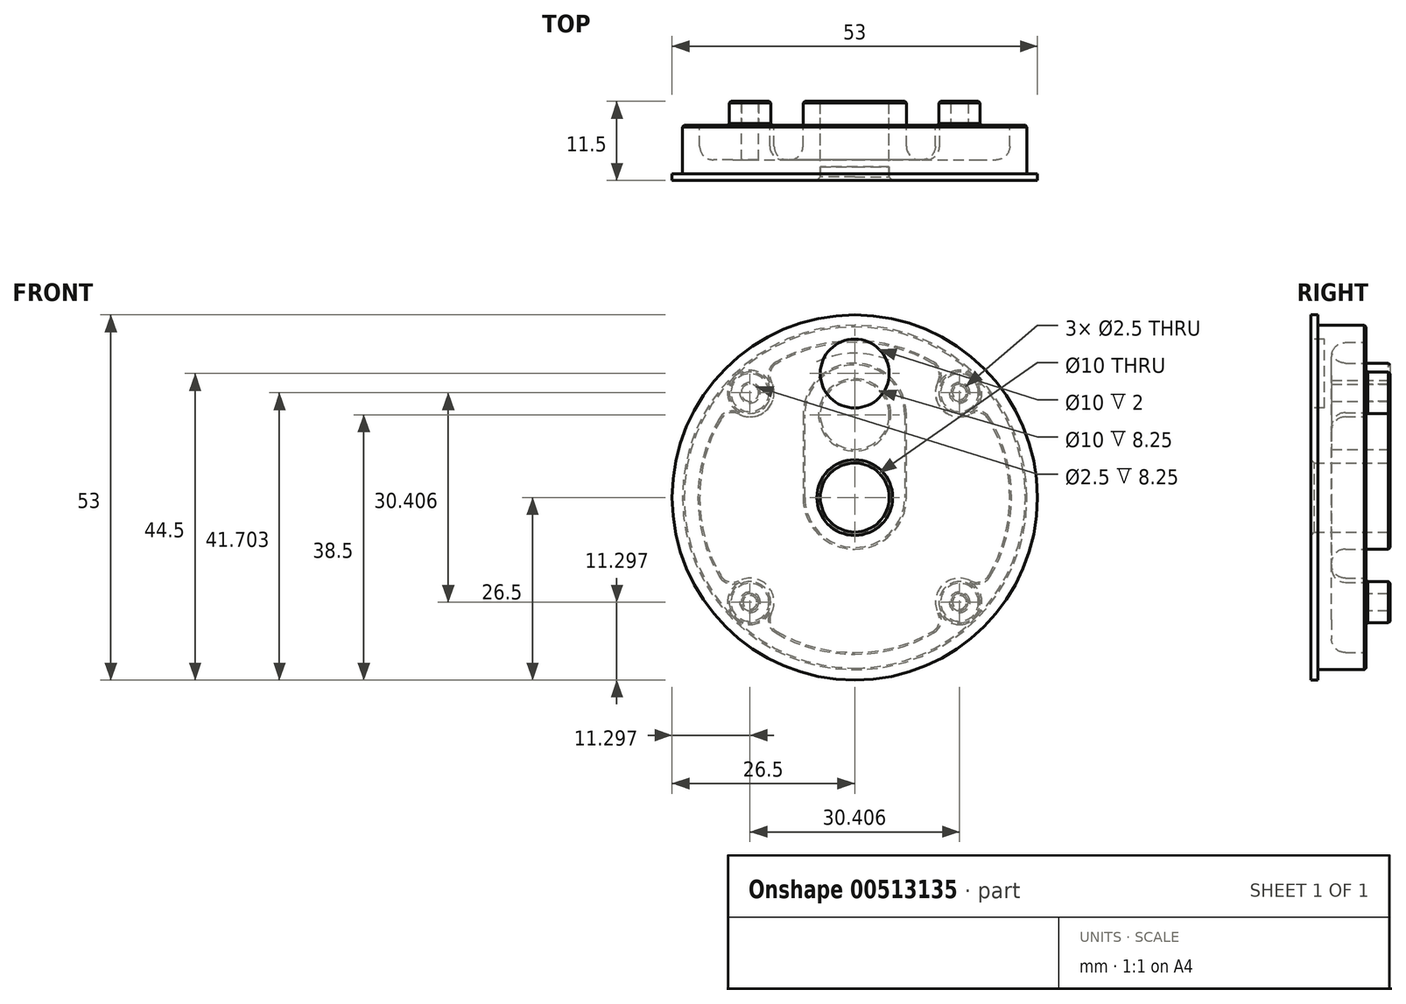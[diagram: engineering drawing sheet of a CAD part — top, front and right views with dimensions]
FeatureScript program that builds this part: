
annotation { "Feature Type Name" : "Feature", "Feature Type Description" : "" }
export const myFeature = defineFeature(function(context is Context, id is Id, definition is map)
    precondition{}
    {
        {
            var Q0;
            Q0=qCreatedBy(makeId("Front.planeOp"),FACE);
            var sketch = newSketch(context, id + "F0", { "sketchPlane" : qUnion([Q0])});
            skCircle(sketch, "E0", {"center": v(0, 0) * mm, "radius": 29.5 * mm});
            skCircle(sketch, "E1", {"center": v(0, 0) * mm, "radius": 25 * mm});
            skSolve(sketch);
        }
        {
            var Q0;
            Q0=makeQuery(id+"F0.imprint","IMPRINT",FACE,{"disambiguationData":[TD([[makeQuery(id+"F0.imprint","IMPRINT",EDGE,{"derivedFrom":sQuery(id+"F0.wireOp",EDGE,"E1")}),1.0]])]});
            extrude(context, id + "F1", {"entities" : qUnion([Q0]), "endBound" : BoundingType.SYMMETRIC, "depth" : 7 * mm});
        }
        {
            var Q0;
            Q0=qCreatedBy(makeId("Top.planeOp"),FACE);
            var sketch = newSketch(context, id + "F2", { "sketchPlane" : qUnion([Q0])});
            skLineSegment(sketch, "E2", {"start": v(0, -12.73) * mm, "end": v(0, 13.03) * mm});
            skSolve(sketch);
        }
        {
            var Q0;
            Q0=qCreatedBy(makeId("Top.planeOp"),FACE);
            var sketch = newSketch(context, id + "F3", { "sketchPlane" : qUnion([Q0])});
            skLineSegment(sketch, "E3", {"start": v(0, 15.7) * mm, "end": v(0, -16.28) * mm});
            skSolve(sketch);
        }
        {
            var Q0;
            Q0=makeQuery(id+"F1.opExtrude","CAP_FACE",FACE,{"disambiguationData":[OSD([sQuery(id+"F0.wireOp",EDGE,"E1")])],"isStart":true});
            var sketch = newSketch(context, id + "F4", { "sketchPlane" : qUnion([Q0])});
            skCircle(sketch, "E4", {"center": v(0, 12) * mm, "radius": 5 * mm});
            skCircle(sketch, "E5", {"center": v(0, 0) * mm, "radius": 5 * mm});
            skSolve(sketch);
        }
        {
            var Q0;
            Q0 = qSketchRegion(id + "F4", true);
            extrude(context, id + "F5", {"entities" : qUnion([Q0]), "operationType" : NewBodyOperationType.REMOVE, "oppositeDirection" : true, "depth" : 5 * mm});
        }
        {
            var Q0;
            Q0=makeQuery(id+"F1.opExtrude","CAP_FACE",FACE,{"disambiguationData":[OSD([sQuery(id+"F0.wireOp",EDGE,"E1")])],"isStart":true});
            var sketch = newSketch(context, id + "F6", { "sketchPlane" : qUnion([Q0])});
            skLineSegment(sketch, "E6", {"start": v(0, 0) * mm, "end": v(0, 12) * mm});
            skLineSegment(sketch, "E7", {"start": v(0, 0) * mm, "end": v(15.2, 15.2) * mm});
            skCircle(sketch, "E8", {"center": v(15.2, 15.2) * mm, "radius": 1.25 * mm});
            skSolve(sketch);
        }
        {
            var Q0;
            Q0 = qSketchRegion(id + "F6", true);
            extrude(context, id + "F7", {"entities" : qUnion([Q0]), "operationType" : NewBodyOperationType.REMOVE, "oppositeDirection" : true, "depth" : 5 * mm});
        }
        {
            var Q0;
            Q0=qCreatedBy(makeId("Top.planeOp"),FACE);
            var sketch = newSketch(context, id + "F8", { "sketchPlane" : qUnion([Q0])});
            skLineSegment(sketch, "E9", {"start": v(0, 16.58) * mm, "end": v(0, -21.32) * mm});
            skSolve(sketch);
        }
        {
            var Q0;
            Q0=makeQuery(id+"F5.boolean.opBoolean","COPY",FACE,{"derivedFrom":makeQuery(id+"F5.opExtrude","CAP_FACE",FACE,{"disambiguationData":[OSD([sQuery(id+"F4.wireOp",EDGE,"E5")])],"isStart":false})});
            var sketch = newSketch(context, id + "F9", { "sketchPlane" : qUnion([Q0])});
            skCircle(sketch, "E10", {"center": v(0, 0) * mm, "radius": 5 * mm});
            skSolve(sketch);
        }
        {
            var Q0;
            Q0=makeQuery(id+"F9.imprint","IMPRINT",FACE,{"disambiguationData":[TD([[makeQuery(id+"F9.imprint","IMPRINT",EDGE,{"derivedFrom":sQuery(id+"F9.wireOp",EDGE,"E10")}),1.0]])]});
            extrude(context, id + "F10", {"entities" : qUnion([Q0]), "operationType" : NewBodyOperationType.REMOVE, "oppositeDirection" : true, "depth" : 25 * mm});
        }
        {
            var Q0;
            Q0=makeQuery(id+"F1.opExtrude","CAP_FACE",FACE,{"disambiguationData":[OSD([sQuery(id+"F0.wireOp",EDGE,"E1")])],"isStart":true});
            var sketch = newSketch(context, id + "F11", { "sketchPlane" : qUnion([Q0])});
            skArc(sketch, "E11", {"start": v(-13.3, -18.14) * mm, "mid": v(0, -22.5) * mm, "end": v(13.3, -18.14) * mm});
            skArc(sketch, "E12", {"start": v(13.3, 18.14) * mm, "mid": v(12.73, 12.73) * mm, "end": v(18.14, 13.3) * mm});
            skArc(sketch, "E13", {"start": v(-18.14, 13.3) * mm, "mid": v(-12.73, 12.73) * mm, "end": v(-13.3, 18.14) * mm});
            skArc(sketch, "E14", {"start": v(-13.3, -18.14) * mm, "mid": v(-12.73, -12.73) * mm, "end": v(-18.14, -13.3) * mm});
            skArc(sketch, "E15", {"start": v(18.14, -13.3) * mm, "mid": v(12.73, -12.73) * mm, "end": v(13.3, -18.14) * mm});
            skArc(sketch, "E16", {"start": v(7.5, 12) * mm, "mid": v(0, 19.5) * mm, "end": v(-7.5, 12) * mm});
            skArc(sketch, "E17", {"start": v(-7.5, 0) * mm, "mid": v(0, -7.5) * mm, "end": v(7.5, 0) * mm});
            skLineSegment(sketch, "E18", {"start": v(-7.5, 12) * mm, "end": v(-7.5, 0) * mm});
            skLineSegment(sketch, "E19", {"start": v(7.5, 12) * mm, "end": v(7.5, 0) * mm});
            skArc(sketch, "E20.trimOffspring", {"start": v(18.14, -13.3) * mm, "mid": v(22.5, 0) * mm, "end": v(18.14, 13.3) * mm});
            skArc(sketch, "E21.trimOffspring", {"start": v(13.3, 18.14) * mm, "mid": v(0, 22.5) * mm, "end": v(-13.3, 18.14) * mm});
            skArc(sketch, "E22.trimOffspring", {"start": v(-18.14, 13.3) * mm, "mid": v(-22.5, 0) * mm, "end": v(-18.14, -13.3) * mm});
            skSolve(sketch);
        }
        {
            var Q0;
            Q0=makeQuery(id+"F11.imprint","IMPRINT",FACE,{"disambiguationData":[TD([[makeQuery(id+"F11.imprint","IMPRINT",EDGE,{"derivedFrom":sQuery(id+"F11.wireOp",EDGE,"E11")}),1.0]])]});
            extrude(context, id + "F12", {"entities" : qUnion([Q0]), "operationType" : NewBodyOperationType.REMOVE, "oppositeDirection" : true, "depth" : 5 * mm});
        }
        {
            var Q0;
            Q0=makeQuery(id+"F12.boolean.opBoolean","COPY",EDGE,{"derivedFrom":makeQuery(id+"F12.opExtrude","SWEPT_EDGE",EDGE,{"disambiguationData":[OSD([sQuery(id+"F11.wireOp",EDGE,"E12"),sQuery(id+"F11.wireOp",EDGE,"E21.trimOffspring")])]})});
            var Q1;
            Q1=makeQuery(id+"F12.boolean.opBoolean","COPY",EDGE,{"derivedFrom":makeQuery(id+"F12.opExtrude","SWEPT_EDGE",EDGE,{"disambiguationData":[OSD([sQuery(id+"F11.wireOp",EDGE,"E11"),sQuery(id+"F11.wireOp",EDGE,"E15")])]})});
            var Q2;
            Q2=makeQuery(id+"F12.boolean.opBoolean","COPY",EDGE,{"derivedFrom":makeQuery(id+"F12.opExtrude","SWEPT_EDGE",EDGE,{"disambiguationData":[OSD([sQuery(id+"F11.wireOp",EDGE,"E13"),sQuery(id+"F11.wireOp",EDGE,"E21.trimOffspring")])]})});
            var Q3;
            Q3=makeQuery(id+"F12.boolean.opBoolean","COPY",EDGE,{"derivedFrom":makeQuery(id+"F12.opExtrude","SWEPT_EDGE",EDGE,{"disambiguationData":[OSD([sQuery(id+"F11.wireOp",EDGE,"E13"),sQuery(id+"F11.wireOp",EDGE,"E22.trimOffspring")])]})});
            var Q4;
            Q4=makeQuery(id+"F12.boolean.opBoolean","COPY",EDGE,{"derivedFrom":makeQuery(id+"F12.opExtrude","SWEPT_EDGE",EDGE,{"disambiguationData":[OSD([sQuery(id+"F11.wireOp",EDGE,"E12"),sQuery(id+"F11.wireOp",EDGE,"E20.trimOffspring")])]})});
            var Q5;
            Q5=makeQuery(id+"F12.boolean.opBoolean","COPY",EDGE,{"derivedFrom":makeQuery(id+"F12.opExtrude","SWEPT_EDGE",EDGE,{"disambiguationData":[OSD([sQuery(id+"F11.wireOp",EDGE,"E15"),sQuery(id+"F11.wireOp",EDGE,"E20.trimOffspring")])]})});
            var Q6;
            Q6=makeQuery(id+"F12.boolean.opBoolean","COPY",EDGE,{"derivedFrom":makeQuery(id+"F12.opExtrude","SWEPT_EDGE",EDGE,{"disambiguationData":[OSD([sQuery(id+"F11.wireOp",EDGE,"E14"),sQuery(id+"F11.wireOp",EDGE,"E22.trimOffspring")])]})});
            var Q7;
            Q7=makeQuery(id+"F12.boolean.opBoolean","COPY",EDGE,{"derivedFrom":makeQuery(id+"F12.opExtrude","SWEPT_EDGE",EDGE,{"disambiguationData":[OSD([sQuery(id+"F11.wireOp",EDGE,"E11"),sQuery(id+"F11.wireOp",EDGE,"E14")])]})});
            fillet(context, id + "F13", {"entities" : qUnion([Q0, Q1, Q2, Q3, Q4, Q5, Q6, Q7]), "radius" : 2 * mm, "tangentPropagation" : true, "allowEdgeOverflow" : false});
        }
        {
            var Q0;
            Q0=makeQuery(id+"F12.boolean.opBoolean","COPY",FACE,{"derivedFrom":makeQuery(id+"F12.opExtrude","CAP_FACE",FACE,{"disambiguationData":[OSD([sQuery(id+"F11.wireOp",EDGE,"E11"),sQuery(id+"F11.wireOp",EDGE,"E12"),sQuery(id+"F11.wireOp",EDGE,"E13"),sQuery(id+"F11.wireOp",EDGE,"E14"),sQuery(id+"F11.wireOp",EDGE,"E15"),sQuery(id+"F11.wireOp",EDGE,"E16"),sQuery(id+"F11.wireOp",EDGE,"E17"),sQuery(id+"F11.wireOp",EDGE,"E18"),sQuery(id+"F11.wireOp",EDGE,"E19"),sQuery(id+"F11.wireOp",EDGE,"E20.trimOffspring"),sQuery(id+"F11.wireOp",EDGE,"E21.trimOffspring"),sQuery(id+"F11.wireOp",EDGE,"E22.trimOffspring")])],"isStart":false})});
            fillet(context, id + "F14", {"entities" : qUnion([Q0]), "radius" : 2 * mm, "tangentPropagation" : true, "allowEdgeOverflow" : false});
        }
        {
            var Q0;
            Q0=makeQuery(id+"F1.opExtrude","CAP_FACE",FACE,{"disambiguationData":[OSD([sQuery(id+"F0.wireOp",EDGE,"E1")])],"isStart":false});
            var sketch = newSketch(context, id + "F15", { "sketchPlane" : qUnion([Q0])});
            skCircle(sketch, "E23", {"center": v(0, 0) * mm, "radius": 26.5 * mm});
            skCircle(sketch, "E24", {"center": v(0, 0) * mm, "radius": 5 * mm});
            skSolve(sketch);
        }
        {
            var Q0;
            Q0 = qSketchRegion(id + "F15", true);
            extrude(context, id + "F16", {"entities" : qUnion([Q0]), "operationType" : NewBodyOperationType.ADD, "depth" : 1 * mm});
        }
        {
            var Q0;
            Q0=makeQuery(id+"F16.opExtrude","CAP_FACE",FACE,{"disambiguationData":[OSD([sQuery(id+"F15.wireOp",EDGE,"E23"),sQuery(id+"F15.wireOp",EDGE,"E24")])],"isStart":false});
            var sketch = newSketch(context, id + "F17", { "sketchPlane" : qUnion([Q0])});
            skCircle(sketch, "E25", {"center": v(0, 18) * mm, "radius": 5 * mm});
            skSolve(sketch);
        }
        {
            var Q0;
            Q0=makeQuery(id+"F17.imprint","IMPRINT",FACE,{"disambiguationData":[TD([[makeQuery(id+"F17.imprint","IMPRINT",EDGE,{"derivedFrom":sQuery(id+"F17.wireOp",EDGE,"E25")}),1.0]])]});
            extrude(context, id + "F18", {"entities" : qUnion([Q0]), "operationType" : NewBodyOperationType.REMOVE, "oppositeDirection" : true, "depth" : 2 * mm});
        }
        {
            var Q0;
            Q0=makeQuery(id+"F12.boolean.opBoolean","SPLIT",FACE,{"disambiguationData":[TD([makeQuery(id+"F5.boolean.opBoolean","COPY",FACE,{"derivedFrom":makeQuery(id+"F5.opExtrude","SWEPT_FACE",FACE,{"disambiguationData":[OSD([sQuery(id+"F4.wireOp",EDGE,"E4")])]})})])],"derivedFrom":makeQuery(id+"F1.opExtrude","CAP_FACE",FACE,{"disambiguationData":[OSD([sQuery(id+"F0.wireOp",EDGE,"E1")])],"isStart":true})});
            var sketch = newSketch(context, id + "F19", { "sketchPlane" : qUnion([Q0])});
            skCircle(sketch, "E26", {"center": v(0, 12) * mm, "radius": 5 * mm});
            skCircle(sketch, "E27", {"center": v(0, 0) * mm, "radius": 5 * mm});
            skArc(sketch, "E28", {"start": v(7.5, 12) * mm, "mid": v(0, 19.5) * mm, "end": v(-7.5, 12) * mm});
            skArc(sketch, "E29", {"start": v(-7.5, 0) * mm, "mid": v(0, -7.5) * mm, "end": v(7.5, 0) * mm});
            skLineSegment(sketch, "E30", {"start": v(7.5, 12) * mm, "end": v(7.5, 0) * mm});
            skLineSegment(sketch, "E31", {"start": v(-7.5, 12) * mm, "end": v(-7.5, 0) * mm});
            skSolve(sketch);
        }
        {
            var Q0;
            Q0 = qSketchRegion(id + "F19", true);
            extrude(context, id + "F20", {"entities" : qUnion([Q0]), "operationType" : NewBodyOperationType.ADD, "depth" : 3.5 * mm});
        }
        {
            var Q0;
            Q0=makeQuery(id+"F16.opExtrude","CAP_EDGE",EDGE,{"disambiguationData":[OSD([sQuery(id+"F15.wireOp",EDGE,"E24")])],"isStart":false});
            chamfer(context, id + "F21", {"entities" : qUnion([Q0]), "width" : 0.5 * mm, "tangentPropagation" : true});
        }
        {
            var Q0;
            {var subQ1=sQuery(id+"F0.wireOp",EDGE,"E1");Q0=makeQuery(id+"F12.boolean.opBoolean","SPLIT",FACE,{"disambiguationData":[TD([makeQuery(id+"F1.opExtrude","SWEPT_FACE",FACE,{"disambiguationData":[OSD([subQ1])]})])],"derivedFrom":makeQuery(id+"F1.opExtrude","CAP_FACE",FACE,{"disambiguationData":[OSD([subQ1])],"isStart":true})});}
            var sketch = newSketch(context, id + "F22", { "sketchPlane" : qUnion([Q0])});
            skCircle(sketch, "E32", {"center": v(15.2, 15.2) * mm, "radius": 3 * mm});
            skCircle(sketch, "E33", {"center": v(15.2, 15.2) * mm, "radius": 1.25 * mm});
            skCircle(sketch, "E34", {"center": v(15.2, -15.2) * mm, "radius": 3 * mm});
            skCircle(sketch, "E35", {"center": v(15.2, -15.2) * mm, "radius": 1.25 * mm});
            skCircle(sketch, "E36", {"center": v(-15.2, -15.2) * mm, "radius": 3 * mm});
            skCircle(sketch, "E37", {"center": v(-15.2, -15.2) * mm, "radius": 1.25 * mm});
            skCircle(sketch, "E38", {"center": v(-15.2, 15.2) * mm, "radius": 3 * mm});
            skCircle(sketch, "E39", {"center": v(-15.2, 15.2) * mm, "radius": 1.25 * mm});
            skSolve(sketch);
        }
        {
            var Q0;
            Q0=makeQuery(id+"F22.imprint","IMPRINT",FACE,{"disambiguationData":[TD([[makeQuery(id+"F22.imprint","IMPRINT",EDGE,{"derivedFrom":sQuery(id+"F22.wireOp",EDGE,"E32")}),1.0]])]});
            var Q1;
            Q1=makeQuery(id+"F22.imprint","IMPRINT",FACE,{"disambiguationData":[TD([[makeQuery(id+"F22.imprint","IMPRINT",EDGE,{"derivedFrom":sQuery(id+"F22.wireOp",EDGE,"E34")}),1.0]])]});
            var Q2;
            Q2=makeQuery(id+"F22.imprint","IMPRINT",FACE,{"disambiguationData":[TD([[makeQuery(id+"F22.imprint","IMPRINT",EDGE,{"derivedFrom":sQuery(id+"F22.wireOp",EDGE,"E38")}),1.0]])]});
            var Q3;
            Q3=makeQuery(id+"F22.imprint","IMPRINT",FACE,{"disambiguationData":[TD([[makeQuery(id+"F22.imprint","IMPRINT",EDGE,{"derivedFrom":sQuery(id+"F22.wireOp",EDGE,"E36")}),1.0]])]});
            extrude(context, id + "F23", {"entities" : qUnion([Q0, Q1, Q2, Q3]), "operationType" : NewBodyOperationType.ADD, "depth" : 3.5 * mm});
        }
        {
            var Q0;
            Q0=makeQuery(id+"F23.opExtrude","CAP_EDGE",EDGE,{"disambiguationData":[OSD([sQuery(id+"F22.wireOp",EDGE,"E36")])],"isStart":false});
            var Q1;
            Q1=makeQuery(id+"F23.opExtrude","CAP_EDGE",EDGE,{"disambiguationData":[OSD([sQuery(id+"F22.wireOp",EDGE,"E37")])],"isStart":false});
            var Q2;
            Q2=makeQuery(id+"F23.opExtrude","CAP_EDGE",EDGE,{"disambiguationData":[OSD([sQuery(id+"F22.wireOp",EDGE,"E34")])],"isStart":false});
            var Q3;
            Q3=makeQuery(id+"F23.opExtrude","CAP_EDGE",EDGE,{"disambiguationData":[OSD([sQuery(id+"F22.wireOp",EDGE,"E35")])],"isStart":false});
            var Q4;
            Q4=makeQuery(id+"F23.opExtrude","CAP_EDGE",EDGE,{"disambiguationData":[OSD([sQuery(id+"F22.wireOp",EDGE,"E38")])],"isStart":false});
            var Q5;
            Q5=makeQuery(id+"F23.opExtrude","CAP_EDGE",EDGE,{"disambiguationData":[OSD([sQuery(id+"F22.wireOp",EDGE,"E39")])],"isStart":false});
            var Q6;
            Q6=makeQuery(id+"F23.opExtrude","CAP_EDGE",EDGE,{"disambiguationData":[OSD([sQuery(id+"F22.wireOp",EDGE,"E33")])],"isStart":false});
            var Q7;
            Q7=makeQuery(id+"F23.opExtrude","CAP_EDGE",EDGE,{"disambiguationData":[OSD([sQuery(id+"F22.wireOp",EDGE,"E32")])],"isStart":false});
            var Q8;
            Q8=makeQuery(id+"F20.opExtrude","CAP_FACE",FACE,{"disambiguationData":[OSD([sQuery(id+"F19.wireOp",EDGE,"E26"),sQuery(id+"F19.wireOp",EDGE,"E27"),sQuery(id+"F19.wireOp",EDGE,"E28"),sQuery(id+"F19.wireOp",EDGE,"E29"),sQuery(id+"F19.wireOp",EDGE,"E30"),sQuery(id+"F19.wireOp",EDGE,"E31")])],"isStart":false});
            chamfer(context, id + "F24", {"entities" : qUnion([Q0, Q1, Q2, Q3, Q4, Q5, Q6, Q7, Q8]), "width" : 0.25 * mm, "tangentPropagation" : true});
        }
        {
            var Q0;
            {var subQ1=sQuery(id+"F0.wireOp",EDGE,"E1");Q0=makeQuery(id+"F12.boolean.opBoolean","SPLIT",FACE,{"disambiguationData":[TD([makeQuery(id+"F1.opExtrude","SWEPT_FACE",FACE,{"disambiguationData":[OSD([subQ1])]})])],"derivedFrom":makeQuery(id+"F1.opExtrude","CAP_FACE",FACE,{"disambiguationData":[OSD([subQ1])],"isStart":true})});}
            chamfer(context, id + "F25", {"entities" : qUnion([Q0]), "width" : 0.25 * mm, "tangentPropagation" : true});
        }
    });
